# Revit family: Hammerkopfschrauben 45 ohne U-Scheibe
name_source: partatom
category: HLS-Bauteile
revit_build: Autodesk Revit 2017 (Build: 20190507_1515(x64)
units: mm (PartAtom-declared; Revit-internal decimal feet)

## family parameters
Arbeitsebenenbasiert = Ja
Beim Laden mit Abzugskörper schneiden = Nein
Bemaßung runder Anschluss = Durchmesser verwenden
Gemeinsam genutzt = Ja
Immer vertikal = Nein
Raumberechnungspunkt = Nein
Teiletyp = Normal

## types (10) — shared parameters
Anzugsmoment XL100 = 0.00 kN-m
Anzugsmoment XL80 = 0.00 kN-m
Breite Hammerkopf = 19 mm
Durchmesser U-Scheibe = 44 mm
Fabrikat = MEFA
Firma = MEFA Befestigungs- und Montagesysteme GmbH
Kurztext1 = Hammerkopf C-Profil 45
L1 = 8 mm  [stored 0.0262467 ft]
Länge Hammerkopf = 40,5 mm
Material = Stahl
Materialname = S235
Mengeneinheit = St
Oberflaeche = galvanisch verzinkt
Profil = C-Profil
Profiltyp = 45
Stärke Hammerkopf = 8 mm
Stärke Scheibe = 3,5 mm
Vorgabe-Ansicht = 1219 mm
vpe = 50 St

## per-type parameters (varying)
| type | Abmessung | Artikelnummer | Baulänge | EAN | Gewicht | Gewicht pro Bauteil | Gewinde | Gewindeplatten 40X22 | Gewindestifte | Kurztext2 | L | Länge Gewinde | NL | Nutzlänge | Sechskantmutter | U-Scheiben |
| Hammerkopfschraube M 8x 35 | M8 x 35 mm mm | 0698735 | 19,5 mm | 4250928415875 | 0.10 kg | 0.10 kg | M8 | MEFA Gewindeplatte 40x22 : MEFA Gewindeplatte 40x22 M 8 | Gewindestifte : Gewindestift M8x35 | M8 x 35 mm | 35 mm  [stored 0.114829 ft] | 35 mm  [stored 0.114829 ft] | 10 mm  [stored 0.0328084 ft] | 9,5 mm | Sechskantmutter : Sechskantmutter M8 | Unterlegscheibe : Unterlegscheibe, verstärkt 8.4x44x3.5 |
| Hammerkopfschraube M 8x 40 | M8 x 40 mm mm | 0698740 | 24,5 mm | 4250928415882 | 0.10 kg | 0.10 kg | M8 | MEFA Gewindeplatte 40x22 : MEFA Gewindeplatte 40x22 M 8 | Gewindestifte : Gewindestift M8x40 | M8 x 40 mm | 40 mm  [stored 0.131234 ft] | 40 mm  [stored 0.131234 ft] | 15 mm | 14,5 mm | Sechskantmutter : Sechskantmutter M8 | Unterlegscheibe : Unterlegscheibe, verstärkt 8.4x44x3.5 |
| Hammerkopfschraube M 8x 50 | M8 x 50 mm mm | 0698750 | 34,5 mm | 4250928415899 | 0.10 kg | 0.10 kg | M8 | MEFA Gewindeplatte 40x22 : MEFA Gewindeplatte 40x22 M 8 | Gewindestifte : Gewindestift M8x50 | M8 x 50 mm | 50 mm  [stored 0.164042 ft] | 50 mm  [stored 0.164042 ft] | 25 mm  [stored 0.082021 ft] | 24,5 mm | Sechskantmutter : Sechskantmutter M8 | Unterlegscheibe : Unterlegscheibe, verstärkt 8.4x44x3.5 |
| Hammerkopfschraube M 8x 70 | M8 x 70 mm mm | 0698770 | 54,5 mm | 4250928415905 | 0.11 kg | 0.11 kg | M8 | MEFA Gewindeplatte 40x22 : MEFA Gewindeplatte 40x22 M 8 | Gewindestifte : Gewindestift M8x70 | M8 x 70 mm | 70 mm  [stored 0.229659 ft] | 70 mm  [stored 0.229659 ft] | 45 mm | 44,5 mm | Sechskantmutter : Sechskantmutter M8 | Unterlegscheibe : Unterlegscheibe, verstärkt 8.4x44x3.5 |
| Hammerkopfschraube M10x 35 | M10 x 35 mm mm | 0699235 | 19,5 mm | 4250928415912 | 0.11 kg | 0.11 kg | M10 | MEFA Gewindeplatte 40x22 : MEFA Gewindeplatte 40x22 M10 | Gewindestifte : Gewindestift M10x35 | M10 x 35 mm | 35 mm  [stored 0.114829 ft] | 35 mm  [stored 0.114829 ft] | 8 mm  [stored 0.0262467 ft] | 8 mm | Sechskantmutter : Sechskantmutter M10 | Unterlegscheibe : Unterlegscheibe, verstärkt 10.5x44x3.5 |
| Hammerkopfschraube M10x 50 | M10 x 50 mm mm | 0699250 | 34,5 mm | 4250928415929 | 0.12 kg | 0.12 kg | M10 | MEFA Gewindeplatte 40x22 : MEFA Gewindeplatte 40x22 M10 | Gewindestifte : Gewindestift M10x50 | M10 x 50 mm | 50 mm  [stored 0.164042 ft] | 50 mm  [stored 0.164042 ft] | 23 mm  [stored 0.0754593 ft] | 23 mm | Sechskantmutter : Sechskantmutter M10 | Unterlegscheibe : Unterlegscheibe, verstärkt 10.5x44x3.5 |
| Hammerkopfschraube M10x 70 | M10 x 50 mm mm | 0699250 | 34,5 mm | 4250928415929 | 0.12 kg | 0.12 kg | M10 | MEFA Gewindeplatte 40x22 : MEFA Gewindeplatte 40x22 M10 | Gewindestifte : Gewindestift M10x70 | M10 x 50 mm | 70 mm  [stored 0.229659 ft] | 50 mm  [stored 0.164042 ft] | 35 mm  [stored 0.114829 ft] | 23 mm | Sechskantmutter : Sechskantmutter M10 | Unterlegscheibe : Unterlegscheibe, verstärkt 10.5x44x3.5 |
| Hammerkopfschraube M12x 40 | M12 x 40 mm mm | 0699740 | 25 mm | 4250928415943 | 0.12 kg | 0.12 kg | M12 | MEFA Gewindeplatte 40x22 : MEFA Gewindeplatte 40x22 M12 | Gewindestifte : Gewindestift M12x40 | M12 x 40 mm | 40 mm  [stored 0.131234 ft] | 40 mm  [stored 0.131234 ft] | 11 mm  [stored 0.0360892 ft] | 11 mm | Sechskantmutter : Sechskantmutter M12 | Unterlegscheibe : Unterlegscheibe, verstärkt 13.5x44x3.5 |
| Hammerkopfschraube M12x 50 | M12 x 50 mm mm | 0699750 | 35 mm | 4250928415950 | 0.13 kg | 0.13 kg | M12 | MEFA Gewindeplatte 40x22 : MEFA Gewindeplatte 40x22 M12 | Gewindestifte : Gewindestift M12x50 | M12 x 50 mm | 50 mm  [stored 0.164042 ft] | 50 mm  [stored 0.164042 ft] | 21 mm  [stored 0.0688976 ft] | 21 mm | Sechskantmutter : Sechskantmutter M12 | Unterlegscheibe : Unterlegscheibe, verstärkt 13.5x44x3.5 |
| Hammerkopfschraube M12x 70 | M12 x 70 mm mm | 0699770 | 55 mm | 4250928415967 | 0.14 kg | 0.14 kg | M12 | MEFA Gewindeplatte 40x22 : MEFA Gewindeplatte 40x22 M12 | Gewindestifte : Gewindestift M12x70 | M12 x 70 mm | 70 mm  [stored 0.229659 ft] | 70 mm  [stored 0.229659 ft] | 41 mm  [stored 0.134514 ft] | 41 mm | Sechskantmutter : Sechskantmutter M12 | Unterlegscheibe : Unterlegscheibe, verstärkt 13.5x44x3.5 |

note: [stored X ft] marks values corroborated as IEEE doubles in the binary element streams (Revit-internal decimal feet)

## geometry (parser evidence)
native form markers: Sweep x3
no freeform markers — native parametric forms only
